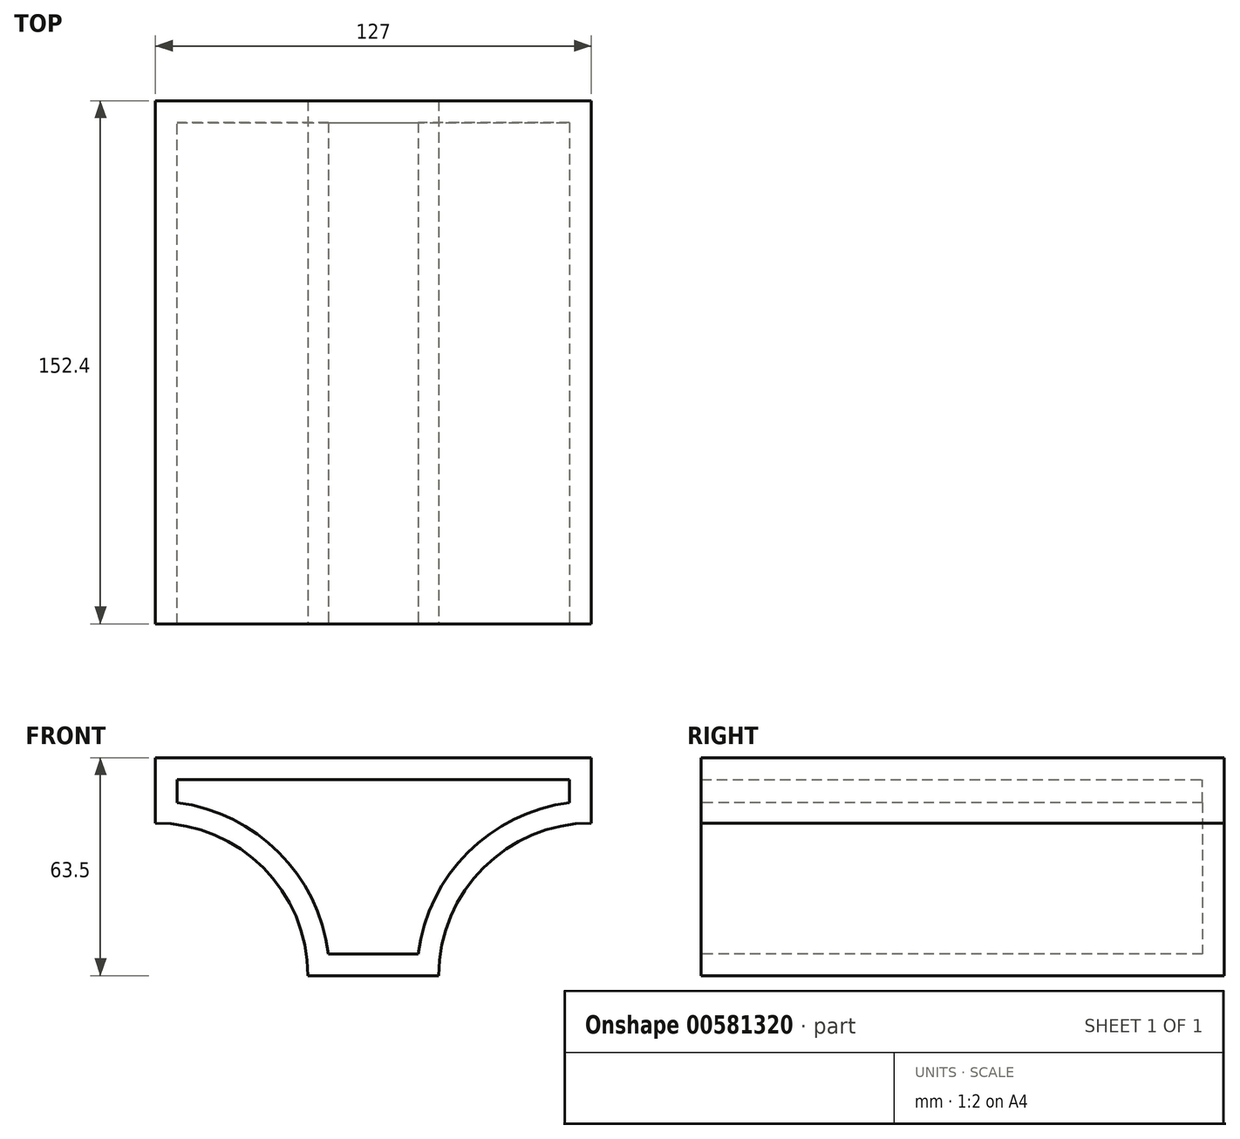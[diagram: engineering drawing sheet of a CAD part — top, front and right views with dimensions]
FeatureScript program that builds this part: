
annotation { "Feature Type Name" : "Feature", "Feature Type Description" : "" }
export const myFeature = defineFeature(function(context is Context, id is Id, definition is map)
    precondition{}
    {
        {
            var Q0;
            Q0=qCreatedBy(makeId("Front.planeOp"),FACE);
            var sketch = newSketch(context, id + "F0", { "sketchPlane" : qUnion([Q0])});
            skLineSegment(sketch, "E0.bottom", {"start": v(-63.5, -31.75) * mm, "end": v(63.5, -31.75) * mm});
            skLineSegment(sketch, "E0.top", {"start": v(-63.5, 31.75) * mm, "end": v(63.5, 31.75) * mm});
            skLineSegment(sketch, "E0.left", {"start": v(-63.5, -31.75) * mm, "end": v(-63.5, 31.75) * mm});
            skLineSegment(sketch, "E0.right", {"start": v(63.5, -31.75) * mm, "end": v(63.5, 31.75) * mm});
            skPoint(sketch, "E0.middle", {"position": v(0, 0) * mm});
            skSolve(sketch);
        }
        {
            var Q0;
            Q0 = qSketchRegion(id + "F0", true);
            extrude(context, id + "F1", {"entities" : qUnion([Q0]), "endBound" : BoundingType.SYMMETRIC, "depth" : 152.4 * mm, "offsetDistance" : 25.4 * mm});
        }
        {
            var Q0;
            Q0=makeQuery(id+"F1.opExtrude","CAP_FACE",FACE,{"disambiguationData":[OSD([sQuery(id+"F0.wireOp",EDGE,"E0.bottom"),sQuery(id+"F0.wireOp",EDGE,"E0.top"),sQuery(id+"F0.wireOp",EDGE,"E0.left"),sQuery(id+"F0.wireOp",EDGE,"E0.right")])],"isStart":false});
            var sketch = newSketch(context, id + "F2", { "sketchPlane" : qUnion([Q0])});
            skArc(sketch, "E1", {"start": v(63.5, 12.7) * mm, "mid": v(32.07, -0.32) * mm, "end": v(19.05, -31.75) * mm});
            skLineSegment(sketch, "E2", {"start": v(19.05, -31.75) * mm, "end": v(63.5, -31.75) * mm});
            skLineSegment(sketch, "E3", {"start": v(63.5, -31.75) * mm, "end": v(63.5, 12.7) * mm});
            skArc(sketch, "E4.MirrorCS", {"start": v(-63.5, 12.7) * mm, "mid": v(-32.07, -0.32) * mm, "end": v(-19.05, -31.75) * mm});
            skLineSegment(sketch, "E5.MirrorCS", {"start": v(-19.05, -31.75) * mm, "end": v(-63.5, -31.75) * mm});
            skLineSegment(sketch, "E6.MirrorCS", {"start": v(-63.5, -31.75) * mm, "end": v(-63.5, 12.7) * mm});
            skSolve(sketch);
        }
        {
            var Q0;
            Q0 = qSketchRegion(id + "F2", true);
            var Q1;
            Q1=makeQuery(id+"F1.opExtrude","CAP_FACE",FACE,{"disambiguationData":[OSD([sQuery(id+"F0.wireOp",EDGE,"E0.bottom"),sQuery(id+"F0.wireOp",EDGE,"E0.top"),sQuery(id+"F0.wireOp",EDGE,"E0.left"),sQuery(id+"F0.wireOp",EDGE,"E0.right")])],"isStart":true});
            extrude(context, id + "F3", {"entities" : qUnion([Q0]), "operationType" : NewBodyOperationType.REMOVE, "endBound" : BoundingType.UP_TO_NEXT, "oppositeDirection" : true, "depth" : 25.4 * mm, "endBoundEntityFace" : qUnion([Q1]), "offsetDistance" : 25.4 * mm});
        }
        {
            var Q0;
            Q0=makeQuery(id+"F1.opExtrude","CAP_FACE",FACE,{"disambiguationData":[OSD([sQuery(id+"F0.wireOp",EDGE,"E0.bottom"),sQuery(id+"F0.wireOp",EDGE,"E0.top"),sQuery(id+"F0.wireOp",EDGE,"E0.left"),sQuery(id+"F0.wireOp",EDGE,"E0.right")])],"isStart":false});
            shell(context, id + "F4", {"entities" : qUnion([Q0]), "thickness" : 6.35 * mm});
        }
    });
